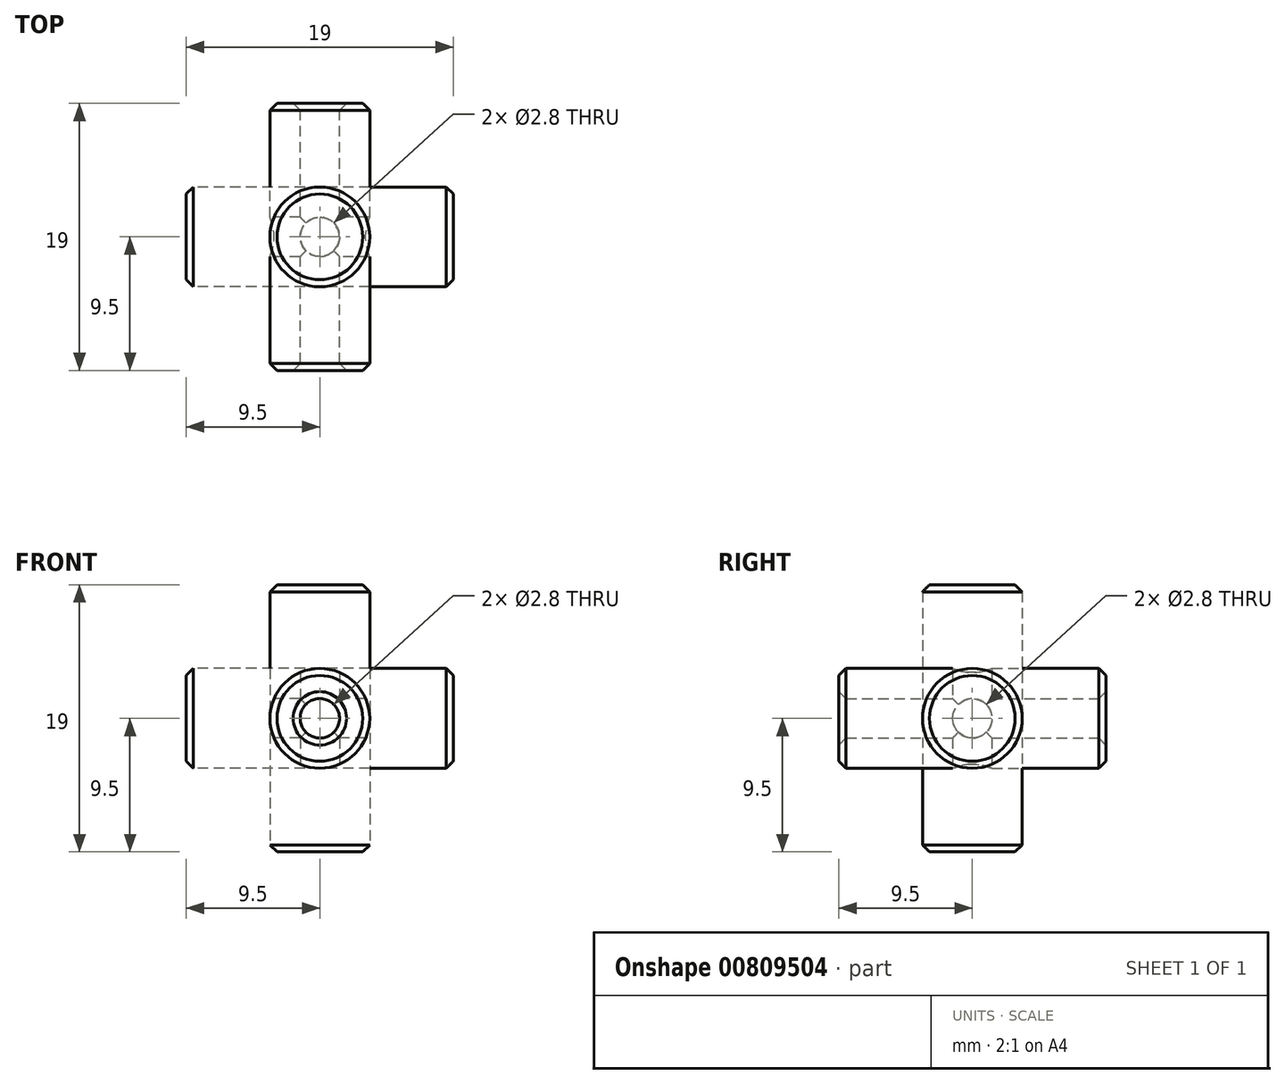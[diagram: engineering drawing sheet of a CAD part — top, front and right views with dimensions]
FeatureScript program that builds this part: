
annotation { "Feature Type Name" : "Feature", "Feature Type Description" : "" }
export const myFeature = defineFeature(function(context is Context, id is Id, definition is map)
    precondition{}
    {
        {
            var Q0;
            Q0=qCreatedBy(makeId("Front.planeOp"),FACE);
            var sketch = newSketch(context, id + "F0", { "sketchPlane" : qUnion([Q0])});
            skCircle(sketch, "E0", {"center": v(0, 0) * mm, "radius": 3.55 * mm});
            skSolve(sketch);
        }
        {
            var Q0;
            Q0 = qSketchRegion(id + "F0", true);
            extrude(context, id + "F1", {"entities" : qUnion([Q0]), "endBound" : BoundingType.SYMMETRIC, "depth" : 19 * mm, "offsetDistance" : 25 * mm});
        }
        {
            var Q0;
            Q0=qCreatedBy(makeId("Front.planeOp"),FACE);
            var sketch = newSketch(context, id + "F2", { "sketchPlane" : qUnion([Q0])});
            skCircle(sketch, "E1", {"center": v(0, 0) * mm, "radius": 1.4 * mm});
            skSolve(sketch);
        }
        {
            var Q0;
            Q0 = qSketchRegion(id + "F2", true);
            extrude(context, id + "F3", {"entities" : qUnion([Q0]), "endBound" : BoundingType.SYMMETRIC, "depth" : 20 * mm, "offsetDistance" : 25 * mm});
        }
        {
            var Q0;
            Q0=qCreatedBy(makeId("Front.planeOp"),FACE);
            var sketch = newSketch(context, id + "F4", { "sketchPlane" : qUnion([Q0])});
            skLineSegment(sketch, "E2.bottom", {"start": v(0, 0) * mm, "end": v(10, 0) * mm});
            skLineSegment(sketch, "E2.top", {"start": v(0, 10) * mm, "end": v(10, 10) * mm});
            skLineSegment(sketch, "E2.left", {"start": v(0, 0) * mm, "end": v(0, 10) * mm});
            skLineSegment(sketch, "E2.right", {"start": v(10, 0) * mm, "end": v(10, 10) * mm});
            skSolve(sketch);
        }
        {
            var Q0;
            Q0 = qSketchRegion(id + "F4", true);
            extrude(context, id + "F5", {"entities" : qUnion([Q0]), "depth" : 10 * mm, "offsetDistance" : 25 * mm});
        }
        {
            var Q0;
            Q0=qCreatedBy(makeId("Origin.pointOp"),VERTEX);
            var Q1;
            Q1=makeQuery(id+"F5.opExtrude","CAP_VERTEX",VERTEX,{"disambiguationData":[OSD([sQuery(id+"F4.wireOp",EDGE,"E2.bottom"),sQuery(id+"F4.wireOp",EDGE,"E2.right")])],"isStart":false});
            var Q2;
            Q2=makeQuery(id+"F5.opExtrude","CAP_VERTEX",VERTEX,{"disambiguationData":[OSD([sQuery(id+"F4.wireOp",EDGE,"E2.top"),sQuery(id+"F4.wireOp",EDGE,"E2.right")])],"isStart":false});
            cPlane(context, id + "F6", {"entities" : qUnion([Q0, Q1, Q2]), "cplaneType" : CPlaneType.THREE_POINT, "offset" : 25 * mm, "width" : 150 * mm, "height" : 150 * mm});
        }
        {
            var Q0;
            Q0=qCreatedBy(id+"F6.planeOp",FACE);
            var sketch = newSketch(context, id + "F7", { "sketchPlane" : qUnion([Q0])});
            skLineSegment(sketch, "E3", {"start": v(0, 0) * mm, "end": v(-14.14, 10) * mm});
            skSolve(sketch);
        }
        {
            var Q0;
            Q0=makeQuery(id+"F5.opExtrude","SWEPT_BODY",BODY,{"disambiguationData":[OSD([sQuery(id+"F4.wireOp",EDGE,"E2.bottom"),sQuery(id+"F4.wireOp",EDGE,"E2.top"),sQuery(id+"F4.wireOp",EDGE,"E2.left"),sQuery(id+"F4.wireOp",EDGE,"E2.right")])]});
            deleteBodies(context, id + "F8", {"entities" : qUnion([Q0])});
        }
        {
            var Q0;
            Q0=makeQuery(id+"F1.opExtrude","SWEPT_BODY",BODY,{"disambiguationData":[OSD([sQuery(id+"F0.wireOp",EDGE,"E0")])]});
            var Q1;
            Q1=makeQuery(id+"F3.opExtrude","SWEPT_BODY",BODY,{"disambiguationData":[OSD([sQuery(id+"F2.wireOp",EDGE,"E1")])]});
            var Q2;
            Q2=sQuery(id+"F7.wireOp",EDGE,"E3");
            circularPattern(context, id + "F9", {"entities" : qUnion([Q0, Q1]), "axis" : qUnion([Q2]), "angle" : 360 * degree, "instanceCount" : 3, "equalSpace" : true});
        }
        {
            var Q0;
            Q0=makeQuery(id+"F9.opPattern","COPY",BODY,{"derivedFrom":makeQuery(id+"F3.opExtrude","SWEPT_BODY",BODY,{"disambiguationData":[OSD([sQuery(id+"F2.wireOp",EDGE,"E1")])]}),"instanceName":"2"});
            var Q1;
            Q1=makeQuery(id+"F9.opPattern","COPY",BODY,{"derivedFrom":makeQuery(id+"F3.opExtrude","SWEPT_BODY",BODY,{"disambiguationData":[OSD([sQuery(id+"F2.wireOp",EDGE,"E1")])]}),"instanceName":"1"});
            var Q2;
            Q2=makeQuery(id+"F3.opExtrude","SWEPT_BODY",BODY,{"disambiguationData":[OSD([sQuery(id+"F2.wireOp",EDGE,"E1")])]});
            var Q3;
            Q3=makeQuery(id+"F1.opExtrude","SWEPT_BODY",BODY,{"disambiguationData":[OSD([sQuery(id+"F0.wireOp",EDGE,"E0")])]});
            booleanBodies(context, id + "F10", {"operationType" : BooleanOperationType.SUBTRACTION, "tools" : qUnion([Q0, Q1, Q2]), "targets" : qUnion([Q3])});
        }
        {
            var Q0;
            Q0=makeQuery(id+"F10.opBoolean","INTERSECT",EDGE,{"derivedFrom":[makeQuery(id+"F1.opExtrude","CAP_FACE",FACE,{"disambiguationData":[OSD([sQuery(id+"F0.wireOp",EDGE,"E0")])],"isStart":true}),makeQuery(id+"F3.opExtrude","SWEPT_FACE",FACE,{"disambiguationData":[OSD([sQuery(id+"F2.wireOp",EDGE,"E1")])]})]});
            var Q1;
            Q1=makeQuery(id+"F1.opExtrude","CAP_EDGE",EDGE,{"disambiguationData":[OSD([sQuery(id+"F0.wireOp",EDGE,"E0")])],"isStart":true});
            var Q2;
            Q2=makeQuery(id+"F9.opPattern","COPY",EDGE,{"derivedFrom":makeQuery(id+"F1.opExtrude","CAP_EDGE",EDGE,{"disambiguationData":[OSD([sQuery(id+"F0.wireOp",EDGE,"E0")])],"isStart":true}),"instanceName":"1"});
            var Q3;
            Q3=makeQuery(id+"F10.opBoolean","INTERSECT",EDGE,{"derivedFrom":[makeQuery(id+"F9.opPattern","COPY",FACE,{"derivedFrom":makeQuery(id+"F1.opExtrude","CAP_FACE",FACE,{"disambiguationData":[OSD([sQuery(id+"F0.wireOp",EDGE,"E0")])],"isStart":true}),"instanceName":"1"}),makeQuery(id+"F9.opPattern","COPY",FACE,{"derivedFrom":makeQuery(id+"F3.opExtrude","SWEPT_FACE",FACE,{"disambiguationData":[OSD([sQuery(id+"F2.wireOp",EDGE,"E1")])]}),"instanceName":"1"})]});
            var Q4;
            Q4=makeQuery(id+"F9.opPattern","COPY",EDGE,{"derivedFrom":makeQuery(id+"F1.opExtrude","CAP_EDGE",EDGE,{"disambiguationData":[OSD([sQuery(id+"F0.wireOp",EDGE,"E0")])],"isStart":false}),"instanceName":"2"});
            var Q5;
            Q5=makeQuery(id+"F10.opBoolean","INTERSECT",EDGE,{"derivedFrom":[makeQuery(id+"F9.opPattern","COPY",FACE,{"derivedFrom":makeQuery(id+"F1.opExtrude","CAP_FACE",FACE,{"disambiguationData":[OSD([sQuery(id+"F0.wireOp",EDGE,"E0")])],"isStart":false}),"instanceName":"2"}),makeQuery(id+"F9.opPattern","COPY",FACE,{"derivedFrom":makeQuery(id+"F3.opExtrude","SWEPT_FACE",FACE,{"disambiguationData":[OSD([sQuery(id+"F2.wireOp",EDGE,"E1")])]}),"instanceName":"2"})]});
            var Q6;
            Q6=makeQuery(id+"F10.opBoolean","INTERSECT",EDGE,{"derivedFrom":[makeQuery(id+"F9.opPattern","COPY",FACE,{"derivedFrom":makeQuery(id+"F1.opExtrude","CAP_FACE",FACE,{"disambiguationData":[OSD([sQuery(id+"F0.wireOp",EDGE,"E0")])],"isStart":true}),"instanceName":"2"}),makeQuery(id+"F9.opPattern","COPY",FACE,{"derivedFrom":makeQuery(id+"F3.opExtrude","SWEPT_FACE",FACE,{"disambiguationData":[OSD([sQuery(id+"F2.wireOp",EDGE,"E1")])]}),"instanceName":"2"})]});
            var Q7;
            Q7=makeQuery(id+"F9.opPattern","COPY",EDGE,{"derivedFrom":makeQuery(id+"F1.opExtrude","CAP_EDGE",EDGE,{"disambiguationData":[OSD([sQuery(id+"F0.wireOp",EDGE,"E0")])],"isStart":true}),"instanceName":"2"});
            var Q8;
            Q8=makeQuery(id+"F9.opPattern","COPY",EDGE,{"derivedFrom":makeQuery(id+"F1.opExtrude","CAP_EDGE",EDGE,{"disambiguationData":[OSD([sQuery(id+"F0.wireOp",EDGE,"E0")])],"isStart":false}),"instanceName":"1"});
            var Q9;
            Q9=makeQuery(id+"F10.opBoolean","INTERSECT",EDGE,{"derivedFrom":[makeQuery(id+"F9.opPattern","COPY",FACE,{"derivedFrom":makeQuery(id+"F1.opExtrude","CAP_FACE",FACE,{"disambiguationData":[OSD([sQuery(id+"F0.wireOp",EDGE,"E0")])],"isStart":false}),"instanceName":"1"}),makeQuery(id+"F9.opPattern","COPY",FACE,{"derivedFrom":makeQuery(id+"F3.opExtrude","SWEPT_FACE",FACE,{"disambiguationData":[OSD([sQuery(id+"F2.wireOp",EDGE,"E1")])]}),"instanceName":"1"})]});
            var Q10;
            Q10=makeQuery(id+"F1.opExtrude","CAP_EDGE",EDGE,{"disambiguationData":[OSD([sQuery(id+"F0.wireOp",EDGE,"E0")])],"isStart":false});
            var Q11;
            Q11=makeQuery(id+"F10.opBoolean","INTERSECT",EDGE,{"derivedFrom":[makeQuery(id+"F1.opExtrude","CAP_FACE",FACE,{"disambiguationData":[OSD([sQuery(id+"F0.wireOp",EDGE,"E0")])],"isStart":false}),makeQuery(id+"F3.opExtrude","SWEPT_FACE",FACE,{"disambiguationData":[OSD([sQuery(id+"F2.wireOp",EDGE,"E1")])]})]});
            chamfer(context, id + "F11", {"entities" : qUnion([Q0, Q1, Q2, Q3, Q4, Q5, Q6, Q7, Q8, Q9, Q10, Q11]), "width" : 0.5 * mm, "tangentPropagation" : true});
        }
    });
